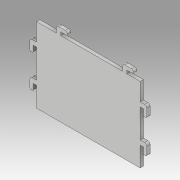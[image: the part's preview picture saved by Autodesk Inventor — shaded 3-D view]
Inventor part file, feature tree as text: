
AUTODESK INVENTOR PART (.ipt)
format: ipt  version: 2019.3 (Build 233278000, 278)  size: 167,424 bytes
history: native  units: mm
features: extrude x1, sketch x1
ambient origin geometry x8: Origin, YZ Plane, XZ Plane, XY Plane, X Axis, Y Axis, Z Axis, Center Point
bodies: Solid1 (feature_tree)
feature tree (2):
  extrude  "Extrusion1"  Depth=68.0mm
  sketch  "Sketch1"  dims[d0=94.0mm d1=68.0mm d2=7.0mm d3=12.0mm d4=12.0mm d7=53.0mm d8=10.0mm d9=3.0mm d10=3.0mm d11=6.0mm d12=18.0mm d13=48.0mm d14=2.0mm d15=1.0mm d16=10.0mm d17=3.0mm d18=3.0mm d19=6.0mm d20=12.0mm d21=72.0mm d22=2.0mm d23=1.0mm d24=3.0mm d25=0.0mm]
